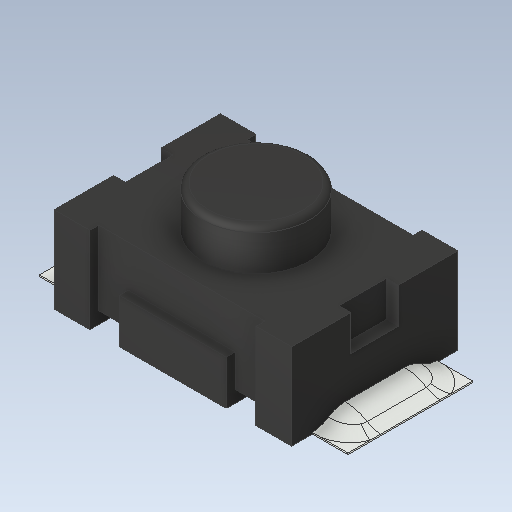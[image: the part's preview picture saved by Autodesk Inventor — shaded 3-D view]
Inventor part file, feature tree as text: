
AUTODESK INVENTOR PART (.ipt)
format: ipt  version: 2020.1 (Build 241239000, 239)  size: 214,528 bytes
history: native  units: mm
features: fillet x1
ambient origin geometry x8: Origin, YZ Plane, XZ Plane, XY Plane, X Axis, Y Axis, Z Axis, Center Point
bodies: Solid1 (feature_tree)
feature tree (1):
  fillet  "Fillet3"  [1 undecoded]
note: 1 required parameter value undecoded (feature->parameter linkage not recoverable at this tier; creation-order binding heuristic only, values carry confidence <= 0.55)
